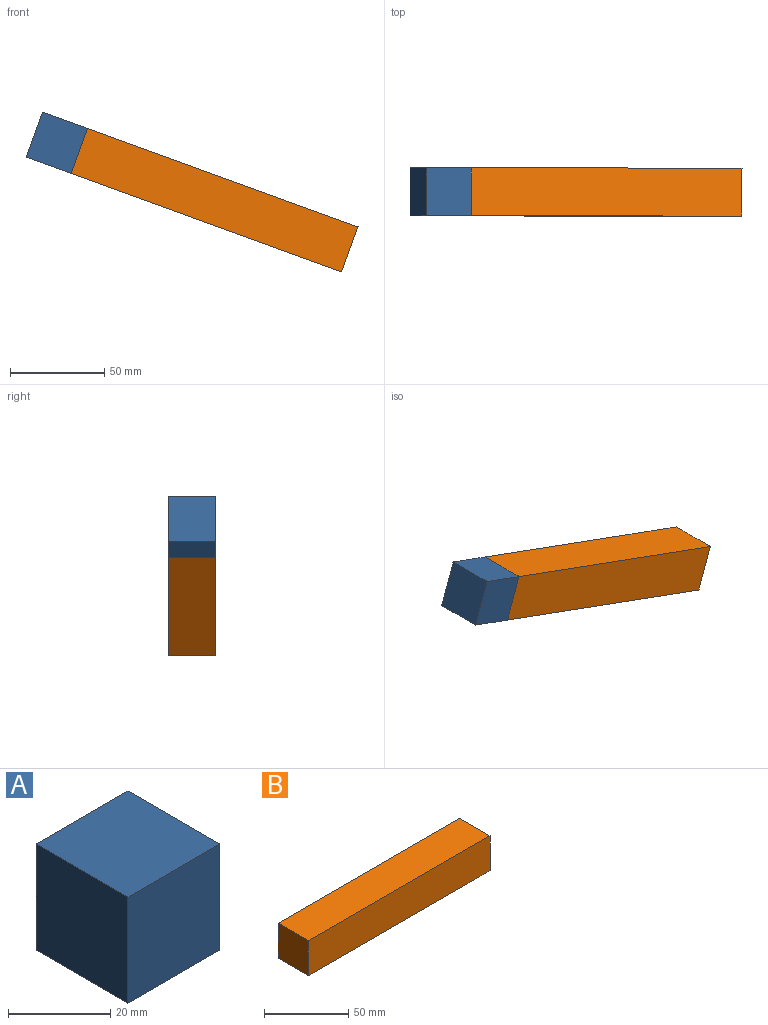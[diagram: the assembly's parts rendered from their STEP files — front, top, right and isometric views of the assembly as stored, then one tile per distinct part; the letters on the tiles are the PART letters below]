
ASSEMBLY  parts=2 mates=1
PART A: 6 faces, bbox 25.4x25.4x25.4 mm
  f0: plane 25.4x25.4mm, normal (0,0,1), area 645.2mm2, adj f1,f3,f4,f5
  f1: plane 25.4x25.4mm, normal (-1,0,0), area 645.2mm2, adj f0,f2,f4,f5
  f2: plane 25.4x25.4mm, normal (0,0,-1), area 645.2mm2, adj f1,f3,f4,f5
  f3: plane 25.4x25.4mm, normal (1,0,0), area 645.2mm2, adj f0,f2,f4,f5
  f4: plane 25.4x25.4mm, normal (0,-1,0), area 645.2mm2, adj f0,f1,f2,f3
  f5: plane 25.4x25.4mm, normal (0,1,0), area 645.2mm2, adj f0,f1,f2,f3
PART B: 6 faces, bbox 152.4x25.4x25.4 mm
  f0: plane 152.4x25.4mm, normal (0,0,1), area 3871mm2, adj f1,f3,f4,f5
  f1: plane 25.4x25.4mm, normal (-1,0,0), area 645.2mm2, adj f0,f2,f4,f5
  f2: plane 152.4x25.4mm, normal (0,0,-1), area 3871mm2, adj f1,f3,f4,f5
  f3: plane 25.4x25.4mm, normal (1,0,0), area 645.2mm2, adj f0,f2,f4,f5
  f4: plane 152.4x25.4mm, normal (0,-1,0), area 3871mm2, adj f0,f1,f2,f3
  f5: plane 152.4x25.4mm, normal (0,1,0), area 3871mm2, adj f0,f1,f2,f3
PLACE A rot(axis=(0,-1,0),160deg) t=(126.85,-16.17,-11.94)mm
PLACE B rot(axis=(0,-1,0),160deg) t=(200.74,-16.17,34.71)mm
MATE slider A.f3 <-> B.f3  axis (-0.94,0,0.34) through (67.45,-28.87,5.31)mm
